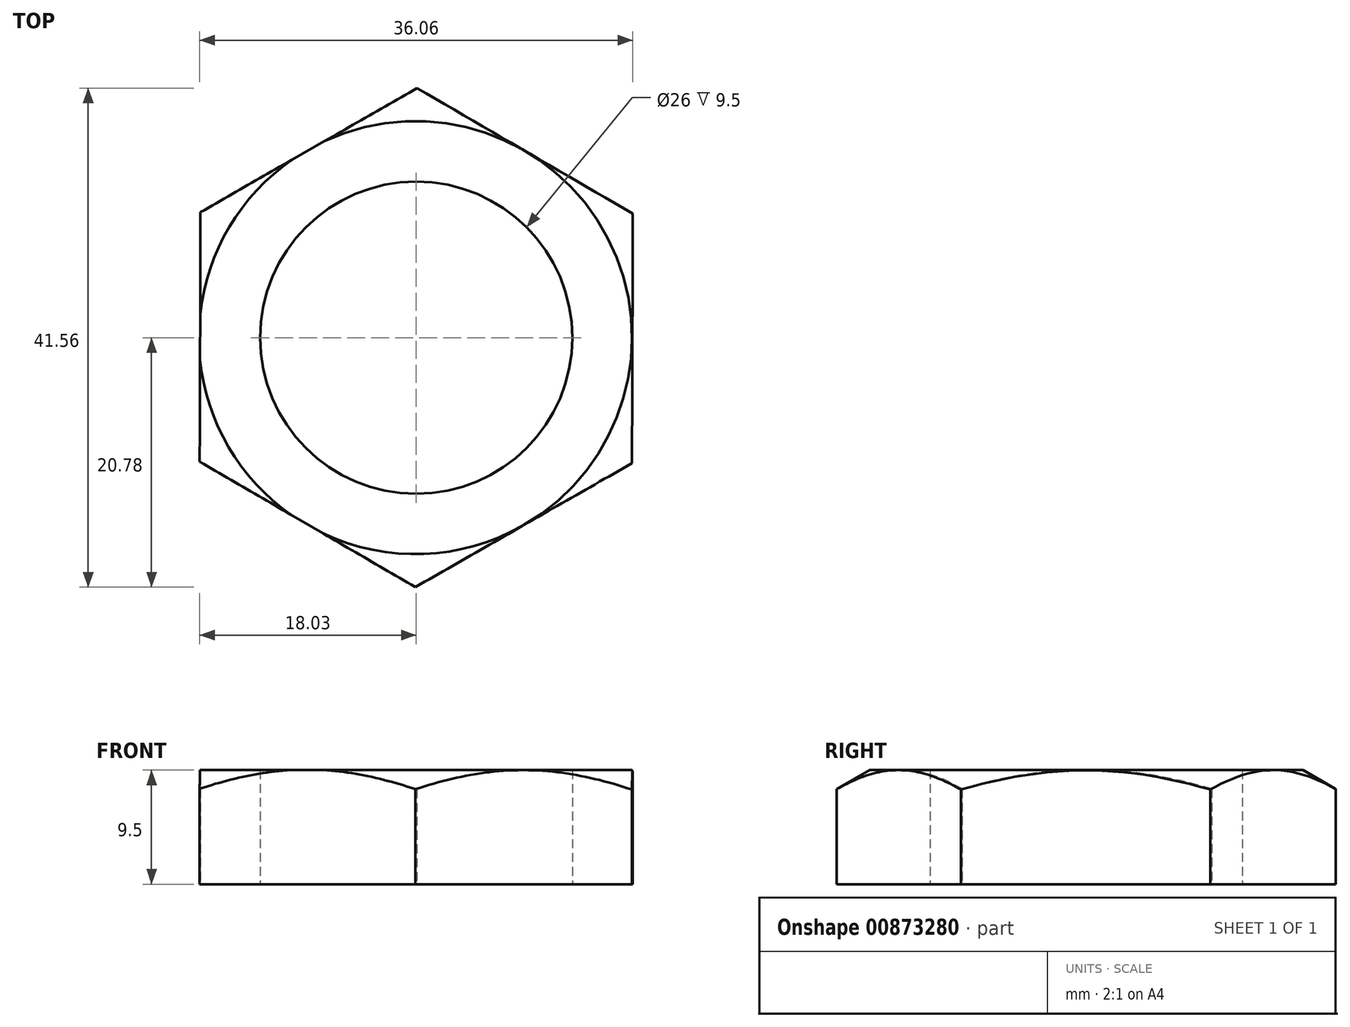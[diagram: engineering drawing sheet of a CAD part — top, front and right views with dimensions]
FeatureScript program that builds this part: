
annotation { "Feature Type Name" : "Feature", "Feature Type Description" : "" }
export const myFeature = defineFeature(function(context is Context, id is Id, definition is map)
    precondition{}
    {
        {
            var Q0;
            Q0=qCreatedBy(makeId("Top.planeOp"),FACE);
            var sketch = newSketch(context, id + "F0", { "sketchPlane" : qUnion([Q0])});
            skCircle(sketch, "E0.cCircle", {"center": v(0, 0) * mm, "radius": 18 * mm, "construction": true});
            skLineSegment(sketch, "E0.0", {"start": v(0.07, 20.78) * mm, "end": v(18.03, 10.33) * mm});
            skLineSegment(sketch, "E0.1", {"start": v(18.03, 10.33) * mm, "end": v(17.97, -10.45) * mm});
            skLineSegment(sketch, "E0.2", {"start": v(17.97, -10.45) * mm, "end": v(-0.07, -20.78) * mm});
            skLineSegment(sketch, "E0.3", {"start": v(-0.07, -20.78) * mm, "end": v(-18.03, -10.33) * mm});
            skLineSegment(sketch, "E0.4", {"start": v(-18.03, -10.33) * mm, "end": v(-17.97, 10.45) * mm});
            skLineSegment(sketch, "E0.5", {"start": v(-17.97, 10.45) * mm, "end": v(0.07, 20.78) * mm});
            skPoint(sketch, "E0.0.midPoint", {"position": v(9.05, 15.56) * mm});
            skCircle(sketch, "E1", {"center": v(0, 0) * mm, "radius": 13 * mm});
            skSolve(sketch);
        }
        {
            var Q0;
            Q0=makeQuery(id+"F0.imprint","IMPRINT",FACE,{"disambiguationData":[TD([[makeQuery(id+"F0.imprint","IMPRINT",EDGE,{"derivedFrom":sQuery(id+"F0.wireOp",EDGE,"E0.0")}),-1.0]])]});
            extrude(context, id + "F1", {"entities" : qUnion([Q0]), "depth" : 9.5 * mm, "offsetDistance" : 25 * mm});
        }
        {
            var Q0;
            Q0=qCreatedBy(makeId("Front.planeOp"),FACE);
            var sketch = newSketch(context, id + "F2", { "sketchPlane" : qUnion([Q0])});
            skLineSegment(sketch, "E2", {"start": v(17.97, 9.5) * mm, "end": v(20.83, 9.5) * mm});
            skLineSegment(sketch, "E3", {"start": v(20.83, 9.5) * mm, "end": v(20.83, 7.85) * mm});
            skLineSegment(sketch, "E4", {"start": v(20.83, 7.85) * mm, "end": v(17.97, 9.5) * mm});
            skLineSegment(sketch, "E5", {"start": v(-0.07, 2.74) * mm, "end": v(-0.07, 13.2) * mm, "construction": true});
            skSolve(sketch);
        }
        {
            var Q0;
            Q0=makeQuery(id+"F2.imprint","IMPRINT",FACE,{"disambiguationData":[TD([[makeQuery(id+"F2.imprint","IMPRINT",EDGE,{"derivedFrom":sQuery(id+"F2.wireOp",EDGE,"E2")}),-1.0]])]});
            var Q1;
            Q1=sQuery(id+"F2.wireOp",EDGE,"E5");
            revolve(context, id + "F3", {"operationType" : NewBodyOperationType.REMOVE, "surfaceOperationType" : NewSurfaceOperationType.NEW, "entities" : qUnion([Q0]), "axis" : qUnion([Q1]), "revolveType" : RevolveType.FULL, "oppositeDirection" : true});
        }
    });
